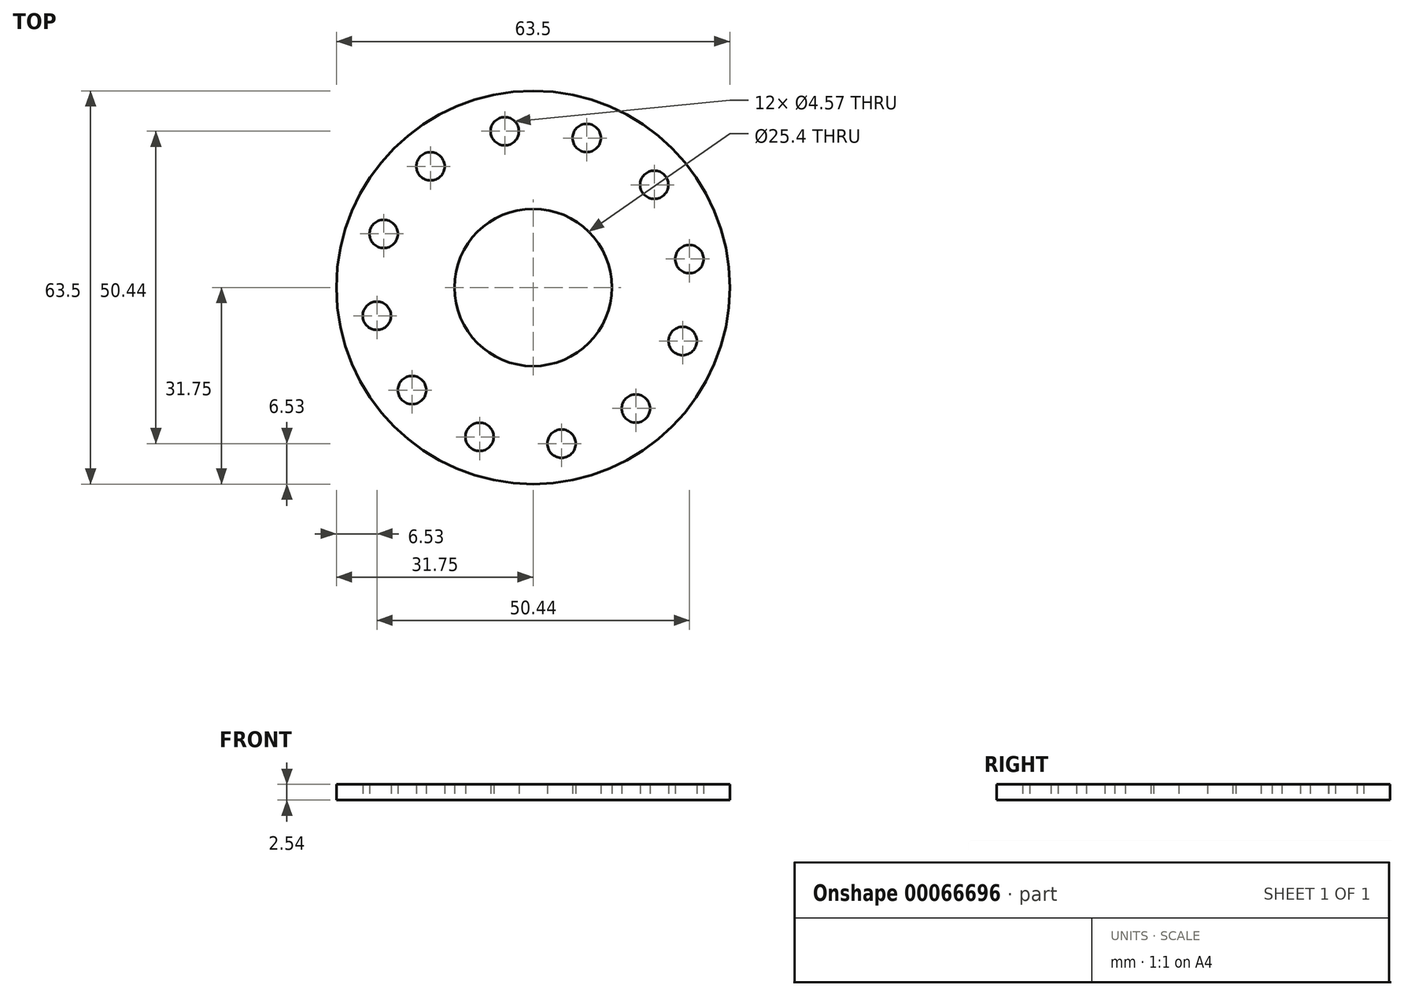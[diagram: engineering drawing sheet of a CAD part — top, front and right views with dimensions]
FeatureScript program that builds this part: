
annotation { "Feature Type Name" : "Feature", "Feature Type Description" : "" }
export const myFeature = defineFeature(function(context is Context, id is Id, definition is map)
    precondition{}
    {
        {
            var Q0;
            Q0=qCreatedBy(makeId("Top.planeOp"),FACE);
            var sketch = newSketch(context, id + "F0", { "sketchPlane" : qUnion([Q0])});
            skCircle(sketch, "E0", {"center": v(0, 0) * mm, "radius": 31.75 * mm});
            skCircle(sketch, "E1", {"center": v(0, 0) * mm, "radius": 12.7 * mm});
            skCircle(sketch, "E2", {"center": v(8.65, 24.13) * mm, "radius": 2.29 * mm});
            skCircle(sketch, "E3.1.0", {"center": v(19.55, 16.57) * mm, "radius": 2.29 * mm});
            skCircle(sketch, "E3.2.0", {"center": v(25.22, 4.58) * mm, "radius": 2.29 * mm});
            skCircle(sketch, "E3.3.0", {"center": v(24.13, -8.65) * mm, "radius": 2.29 * mm});
            skCircle(sketch, "E3.4.0", {"center": v(16.57, -19.55) * mm, "radius": 2.29 * mm});
            skCircle(sketch, "E3.5.0", {"center": v(4.58, -25.22) * mm, "radius": 2.29 * mm});
            skCircle(sketch, "E3.6.0", {"center": v(-8.65, -24.13) * mm, "radius": 2.29 * mm});
            skCircle(sketch, "E3.7.0", {"center": v(-19.55, -16.57) * mm, "radius": 2.29 * mm});
            skCircle(sketch, "E3.8.0", {"center": v(-25.22, -4.58) * mm, "radius": 2.29 * mm});
            skCircle(sketch, "E3.9.0", {"center": v(-24.13, 8.65) * mm, "radius": 2.29 * mm});
            skCircle(sketch, "E3.10.0", {"center": v(-16.57, 19.55) * mm, "radius": 2.29 * mm});
            skCircle(sketch, "E3.11.0", {"center": v(-4.58, 25.22) * mm, "radius": 2.29 * mm});
            skLineSegment(sketch, "E3.anchor1", {"start": v(0, 0) * mm, "end": v(8.65, 24.13) * mm, "construction": true});
            skLineSegment(sketch, "E3.anchor2", {"start": v(0, 0) * mm, "end": v(-4.58, 25.22) * mm, "construction": true});
            skSolve(sketch);
        }
        {
            var Q0;
            Q0=makeQuery(id+"F0.imprint","IMPRINT",FACE,{"disambiguationData":[TD([[makeQuery(id+"F0.imprint","IMPRINT",EDGE,{"derivedFrom":sQuery(id+"F0.wireOp",EDGE,"E0")}),1.0]])]});
            extrude(context, id + "F1", {"entities" : qUnion([Q0]), "depth" : 2.54 * mm});
        }
    });
